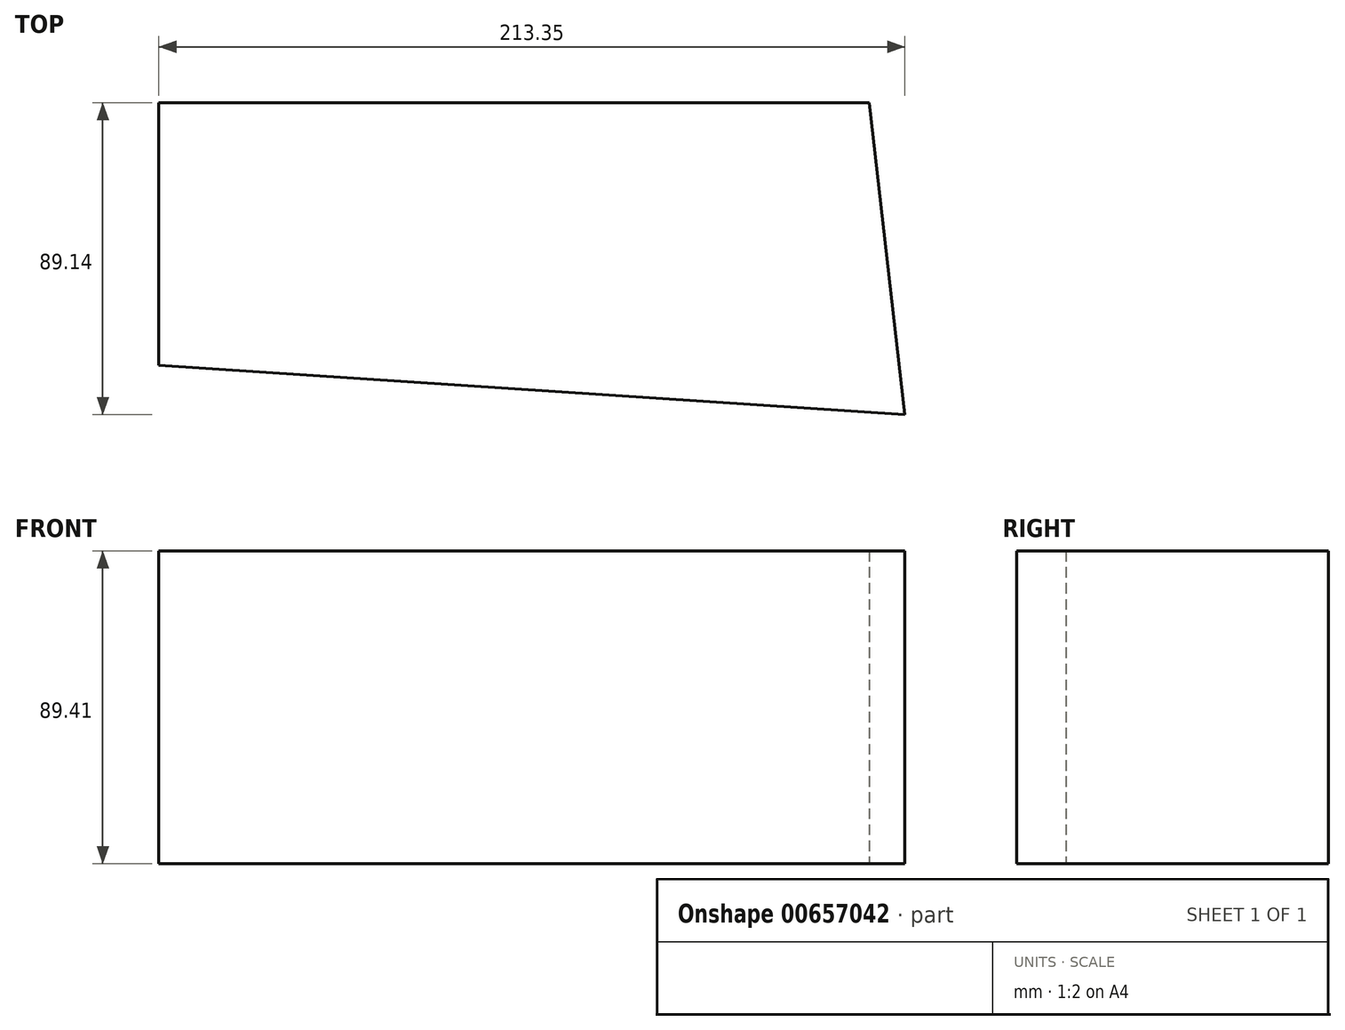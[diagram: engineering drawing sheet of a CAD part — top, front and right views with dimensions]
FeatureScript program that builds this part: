
annotation { "Feature Type Name" : "Feature", "Feature Type Description" : "" }
export const myFeature = defineFeature(function(context is Context, id is Id, definition is map)
    precondition{}
    {
        {
            var Q0;
            Q0=qCreatedBy(makeId("Top.planeOp"),FACE);
            var sketch = newSketch(context, id + "F0", { "sketchPlane" : qUnion([Q0])});
            skLineSegment(sketch, "E0", {"start": v(120.82, -31.1) * mm, "end": v(110.68, 58.04) * mm});
            skLineSegment(sketch, "E1", {"start": v(110.68, 58.04) * mm, "end": v(-92.53, 58.04) * mm});
            skLineSegment(sketch, "E2", {"start": v(-92.53, 58.04) * mm, "end": v(-92.53, -16.99) * mm});
            skPoint(sketch, "E3.start.orphan", {"position": v(-102.61, -16.99) * mm});
            skLineSegment(sketch, "E4", {"start": v(-92.53, -16.99) * mm, "end": v(120.82, -31.1) * mm});
            skSolve(sketch);
        }
        {
            var Q0;
            Q0 = qSketchRegion(id + "F0", true);
            extrude(context, id + "F1", {"entities" : qUnion([Q0]), "depth" : 89.4 * mm, "offsetDistance" : 25.4 * mm});
        }
    });
